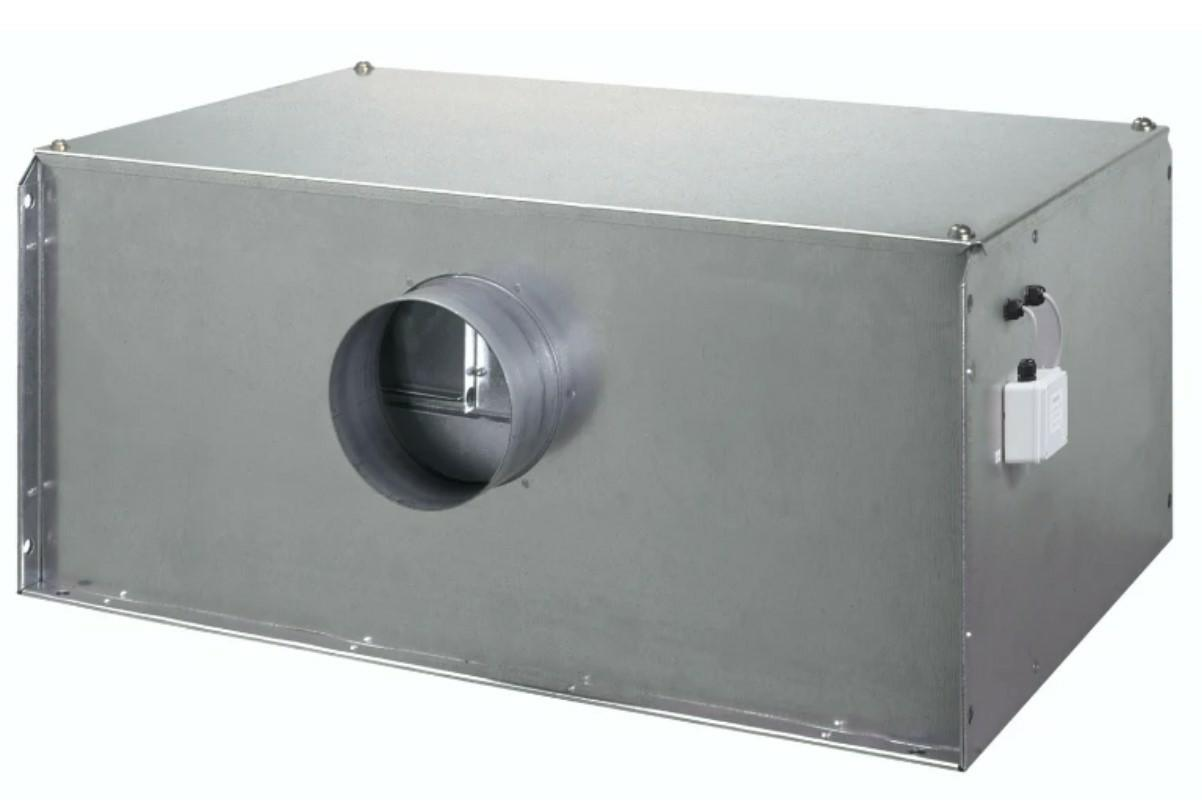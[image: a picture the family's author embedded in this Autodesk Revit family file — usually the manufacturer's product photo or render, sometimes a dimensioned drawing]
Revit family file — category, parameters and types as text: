
# Revit family: CADS_Vent-Axia_MechEquip_Fan_ATQ - SUPPLY
name_source: partatom
category: Mechanical Equipment
units: mm (PartAtom-declared; Revit-internal decimal feet)

## family parameters
Classification = None
Cut with Voids When Loaded = No
Host = Face
OmniClass Number = 23.75.35.17.11
OmniClass Title = Fans for Air Ductwork
Part Type = Normal
Room Calculation Point = No
Round Connector Dimension = Use Diameter
Shared = No

## types (9) — shared parameters
AirflowRateRange = 0.0 L/s
AssemblyPlace = UNKNOWN
AssetType = FIXED
Default Elevation = 1219 mm
DurationUnit = Year
ExteriorInsulation = No
Fitting Type = Ignore
GrossWeight = 0.00 kg
HasProtectiveEarth = No
IsExtendedWarranty = No
ManufacturerAddress = Fleming Way
Crawley 
RH10 9YX
Quantity = 1
RatedCurrent = 0 A
RatedVoltage = 0 V
Status = New
WorkingPressure = 0.0 Pa
zero-valued in all types: CADS_Index, CADS_Usage, ExpectedServiceLife, H, NumberOfPoles, OutOffset, W

## per-type parameters (varying)
| type | EBHoffset | EBVoffset | L | ModelNumber | ModelReference | NominalDiameter | NominalHeight | NominalLength | NominalWidth | Size | SpigotCLHeight | Type Image |
| ATQ10012D | 206 mm | 80 mm | 590 mm  [stored 1.9357 ft] | ATQ31512LD | TWIN ACOUSTIC BOX FAN, 315 DIA SPIGOTS | 100 mm  [stored 0.328084 ft] | 256 mm  [stored 0.839895 ft] | 610 mm  [stored 2.00131 ft] | 622 mm  [stored 2.04068 ft] | 935mm x892mm x426mm | 128 mm  [stored 0.419948 ft] | <None> |
| ATQ12512D | 206 mm | 80 mm | 590 mm  [stored 1.9357 ft] | ATQ12512D | TWIN ACOUSTIC BOX FAN, 125 DIA SPIGOTS | 125 mm  [stored 0.410105 ft] | 256 mm  [stored 0.839895 ft] | 610 mm  [stored 2.00131 ft] | 622 mm  [stored 2.04068 ft] | 610mm x622mm x256mm | 128 mm  [stored 0.419948 ft] | <None> |
| ATQ15012D | 206 mm | 80 mm | 590 mm  [stored 1.9357 ft] | ATQ15012D | TWIN ACOUSTIC BOX FAN, 150 DIA SPIGOTS | 150 mm | 256 mm  [stored 0.839895 ft] | 610 mm  [stored 2.00131 ft] | 622 mm  [stored 2.04068 ft] | 610mm x622mm x256mm | 128 mm  [stored 0.419948 ft] | <None> |
| ATQ16012D | 206 mm | 80 mm | 590 mm  [stored 1.9357 ft] | ATQ16012D | TWIN ACOUSTIC BOX FAN, 160 DIA SPIGOTS | 160 mm  [stored 0.524934 ft] | 256 mm  [stored 0.839895 ft] | 610 mm  [stored 2.00131 ft] | 622 mm  [stored 2.04068 ft] | 610mm x622mm x256mm | 128 mm  [stored 0.419948 ft] | <None> |
| ATQ20012D | 251 mm | 131 mm | 781 mm | ATQ20012D | TWIN ACOUSTIC BOX FAN, 200 DIA SPIGOTS | 200 mm  [stored 0.656168 ft] | 343 mm  [stored 1.12533 ft] | 801 mm  [stored 2.62795 ft] | 734 mm  [stored 2.40814 ft] | 801mm x734mm x343mm | 172 mm | <None> |
| ATQ25012D | 313 mm | 143 mm | 905 mm  [stored 2.96916 ft] | ATQ25012D | TWIN ACOUSTIC BOX FAN, 250 DIA SPIGOTS | 250 mm  [stored 0.82021 ft] | 354 mm  [stored 1.16142 ft] | 925 mm | 829 mm  [stored 2.71982 ft] | 925mm x829mm x354mm | 177 mm  [stored 0.580709 ft] | <None> |
| ATQ31512LD | 361 mm | 207 mm | 915 mm  [stored 3.00197 ft] | ATQ31512LD | TWIN ACOUSTIC BOX FAN, 315 DIA SPIGOTS | 315 mm  [stored 1.03346 ft] | 426 mm  [stored 1.39764 ft] | 935 mm | 892 mm  [stored 2.92651 ft] | 935mm x892mm x426mm | 213 mm  [stored 0.698819 ft] | <None> |
| ATQ31514HD | 375 mm | 285 mm | 1235 mm | ATQ31514HD | TWIN ACOUSTIC BOX FAN, 315 DIA SPIGOTS | 315 mm  [stored 1.03346 ft] | 536 mm | 1255 mm | 1176 mm | 1255mm x1176mm x536mm | 268 mm | <None> |
| ATQ40014D | 377 mm | 285 mm | 1235 mm | ATQ40014D | TWIN ACOUSTIC BOX FAN, 400 DIA SPIGOTS | 400 mm  [stored 1.31234 ft] | 536 mm | 1255 mm | 1176 mm | 1255mm x1176mm x536mm | 268 mm | CADS_Vent-Axia_MechEquip_Fan_ATQ.jpg |

note: [stored X ft] marks values corroborated as IEEE doubles in the binary element streams (Revit-internal decimal feet)

## geometry (parser evidence)
native form markers: Sweep x4
no freeform markers — native parametric forms only
